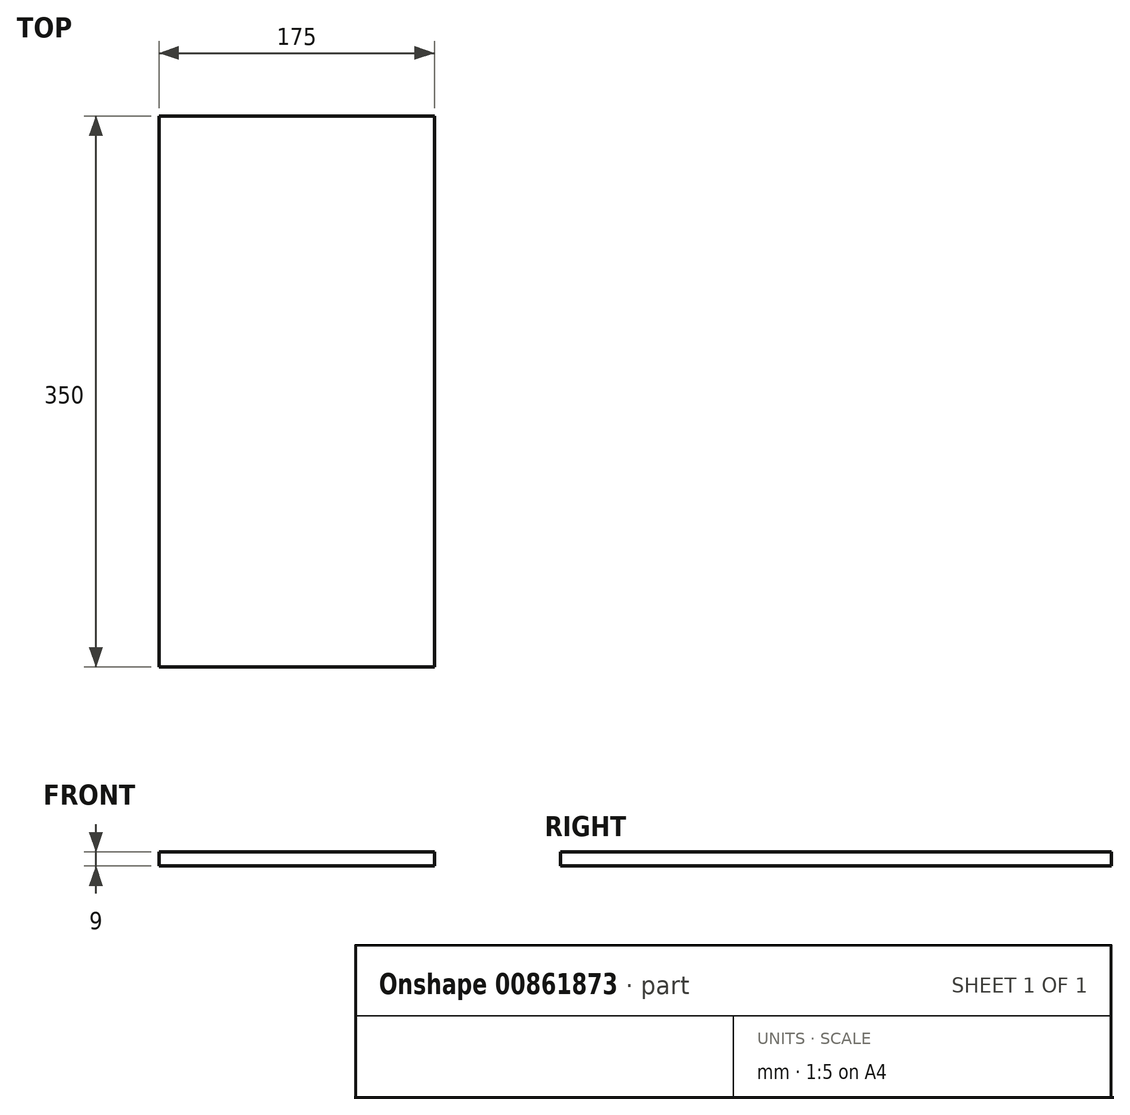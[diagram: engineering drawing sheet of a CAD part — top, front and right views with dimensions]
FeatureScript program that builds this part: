
annotation { "Feature Type Name" : "Feature", "Feature Type Description" : "" }
export const myFeature = defineFeature(function(context is Context, id is Id, definition is map)
    precondition{}
    {
        {
            var Q0;
            Q0=qCreatedBy(makeId("Top.planeOp"),FACE);
            var sketch = newSketch(context, id + "F0", { "sketchPlane" : qUnion([Q0])});
            skLineSegment(sketch, "E0.bottom", {"start": v(87.5, 175) * mm, "end": v(-87.5, 175) * mm});
            skLineSegment(sketch, "E0.top", {"start": v(87.5, -175) * mm, "end": v(-87.5, -175) * mm});
            skLineSegment(sketch, "E0.left", {"start": v(87.5, 175) * mm, "end": v(87.5, -175) * mm});
            skLineSegment(sketch, "E0.right", {"start": v(-87.5, 175) * mm, "end": v(-87.5, -175) * mm});
            skPoint(sketch, "E0.middle", {"position": v(0, 0) * mm});
            skSolve(sketch);
        }
        {
            var Q0;
            Q0 = qSketchRegion(id + "F0", true);
            extrude(context, id + "F1", {"entities" : qUnion([Q0]), "depth" : 9 * mm, "offsetDistance" : 25 * mm});
        }
    });
